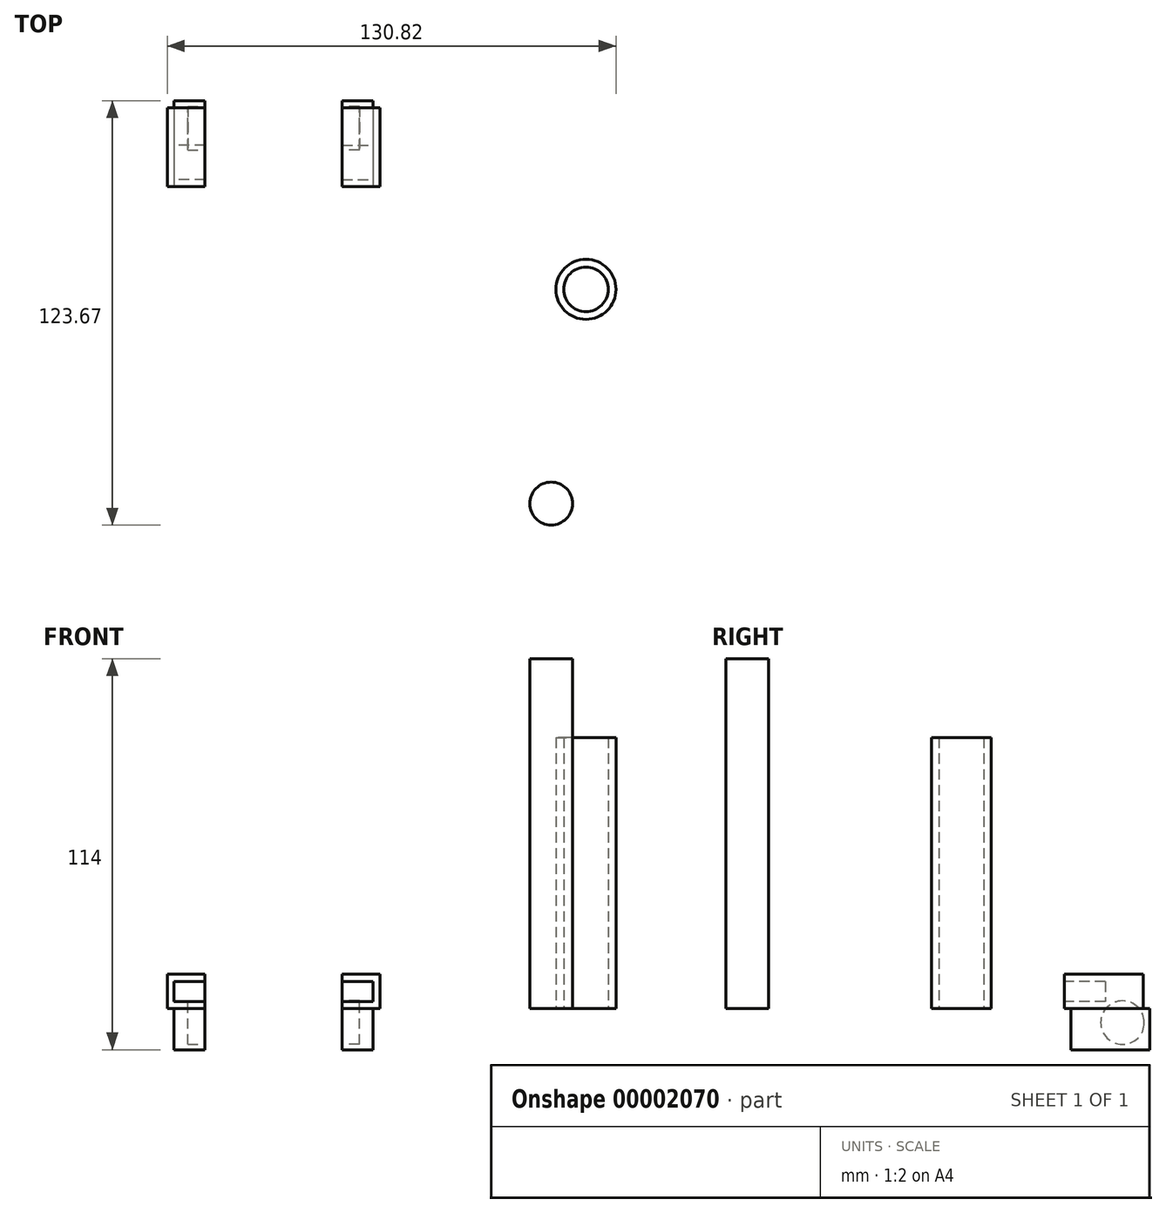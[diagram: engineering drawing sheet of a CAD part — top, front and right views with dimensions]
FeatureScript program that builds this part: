
annotation { "Feature Type Name" : "Feature", "Feature Type Description" : "" }
export const myFeature = defineFeature(function(context is Context, id is Id, definition is map)
    precondition{}
    {
        {
            var Q0;
            Q0=qCreatedBy(makeId("Top.planeOp"),FACE);
            var sketch = newSketch(context, id + "F0", { "sketchPlane" : qUnion([Q0])});
            skLineSegment(sketch, "E0.bottom", {"start": v(-59.77, 61) * mm, "end": v(-48.77, 61) * mm});
            skLineSegment(sketch, "E0.top", {"start": v(-59.77, 46) * mm, "end": v(-48.77, 46) * mm});
            skLineSegment(sketch, "E0.left", {"start": v(-59.77, 61) * mm, "end": v(-59.77, 46) * mm});
            skLineSegment(sketch, "E0.right", {"start": v(-48.77, 61) * mm, "end": v(-48.77, 46) * mm});
            skSolve(sketch);
        }
        {
            var Q0;
            Q0=makeQuery(id+"F0.imprint","IMPRINT",FACE,{"disambiguationData":[TD([[makeQuery(id+"F0.imprint","IMPRINT",EDGE,{"derivedFrom":sQuery(id+"F0.wireOp",EDGE,"E0.bottom")}),-1.0]])]});
            extrude(context, id + "F1", {"entities" : qUnion([Q0]), "depth" : 10 * mm});
        }
        {
            var Q0;
            Q0=makeQuery(id+"F1.opExtrude","SWEPT_FACE",FACE,{"disambiguationData":[OSD([sQuery(id+"F0.wireOp",EDGE,"E0.top")])]});
            var sketch = newSketch(context, id + "F2", { "sketchPlane" : qUnion([Q0])});
            skPoint(sketch, "E1", {"position": v(-48.77, 5) * mm});
            skLineSegment(sketch, "E2", {"start": v(-48.77, 5) * mm, "end": v(-48.77, 7.9) * mm});
            skLineSegment(sketch, "E3", {"start": v(-48.77, 5) * mm, "end": v(-48.77, 2.1) * mm});
            skLineSegment(sketch, "E4", {"start": v(-48.77, 7.9) * mm, "end": v(-57.77, 7.9) * mm});
            skLineSegment(sketch, "E5", {"start": v(-57.77, 7.9) * mm, "end": v(-57.77, 2.1) * mm});
            skLineSegment(sketch, "E6", {"start": v(-57.77, 2.1) * mm, "end": v(-48.77, 2.1) * mm});
            skSolve(sketch);
        }
        {
            var Q0;
            Q0=makeQuery(id+"F2.imprint","IMPRINT",FACE,{"disambiguationData":[TD([[makeQuery(id+"F2.imprint","IMPRINT",EDGE,{"derivedFrom":sQuery(id+"F2.wireOp",EDGE,"E2")}),-1.0]])]});
            extrude(context, id + "F3", {"entities" : qUnion([Q0]), "operationType" : NewBodyOperationType.REMOVE, "oppositeDirection" : true, "depth" : 12 * mm});
        }
        {
            var Q0;
            Q0=makeQuery(id+"F1.opExtrude","CAP_FACE",FACE,{"disambiguationData":[OSD([sQuery(id+"F0.wireOp",EDGE,"E0.bottom"),sQuery(id+"F0.wireOp",EDGE,"E0.top"),sQuery(id+"F0.wireOp",EDGE,"E0.left"),sQuery(id+"F0.wireOp",EDGE,"E0.right")])],"isStart":true});
            var sketch = newSketch(context, id + "F4", { "sketchPlane" : qUnion([Q0])});
            skPoint(sketch, "E7", {"position": v(-48.77, -58) * mm});
            skPoint(sketch, "E8", {"position": v(-57.77, -58) * mm});
            skLineSegment(sketch, "E9.top", {"start": v(-48.77, -48) * mm, "end": v(-57.77, -48) * mm});
            skLineSegment(sketch, "E9.left", {"start": v(-48.77, -58) * mm, "end": v(-48.77, -48) * mm});
            skLineSegment(sketch, "E9.right", {"start": v(-57.77, -58) * mm, "end": v(-57.77, -48) * mm});
            skLineSegment(sketch, "E10", {"start": v(-48.77, -58) * mm, "end": v(-48.77, -63) * mm});
            skLineSegment(sketch, "E11", {"start": v(-48.77, -63) * mm, "end": v(-48.77, -71) * mm});
            skLineSegment(sketch, "E12", {"start": v(-48.77, -71) * mm, "end": v(-57.77, -71) * mm});
            skLineSegment(sketch, "E13", {"start": v(-57.77, -71) * mm, "end": v(-57.77, -57.53) * mm});
            skSolve(sketch);
        }
        {
            var Q0;
            {var subQ5=sQuery(id+"F4.wireOp",EDGE,"E12");Q0=makeQuery(id+"F4.imprint","IMPRINT",FACE,{"disambiguationData":[TD([[makeQuery(id+"F4.imprint","IMPRINT",EDGE,{"derivedFrom":subQ5}),-1.0]])]});}
            var Q1;
            Q1=makeQuery(id+"F4.imprint","IMPRINT",FACE,{"disambiguationData":[TD([[makeQuery(id+"F4.imprint","IMPRINT",EDGE,{"derivedFrom":sQuery(id+"F4.wireOp",EDGE,"E9.top")}),1.0]])]});
            extrude(context, id + "F5", {"entities" : qUnion([Q0, Q1]), "operationType" : NewBodyOperationType.ADD, "depth" : 12 * mm});
        }
        {
            var Q0;
            Q0=makeQuery(id+"F5.boolean.opBoolean","MERGE",FACE,{"derivedFrom":[makeQuery(id+"F1.opExtrude","SWEPT_FACE",FACE,{"disambiguationData":[OSD([sQuery(id+"F0.wireOp",EDGE,"E0.right")])]}),makeQuery(id+"F5.opExtrude","SWEPT_FACE",FACE,{"disambiguationData":[OSD([sQuery(id+"F4.wireOp",EDGE,"E9.left"),sQuery(id+"F4.wireOp",EDGE,"E10")])]})]});
            var sketch = newSketch(context, id + "F6", { "sketchPlane" : qUnion([Q0])});
            skPoint(sketch, "E14", {"position": v(58, -4.1) * mm});
            skPoint(sketch, "E15", {"position": v(58, 7.9) * mm});
            skPoint(sketch, "E16", {"position": v(48, 7.9) * mm});
            skPoint(sketch, "E17", {"position": v(63, 7.9) * mm});
            skPoint(sketch, "E18", {"position": v(63, -4.1) * mm});
            skPoint(sketch, "E19", {"position": v(48, -4.1) * mm});
            skCircle(sketch, "E20", {"center": v(63, -4.1) * mm, "radius": 6.35 * mm});
            skCircle(sketch, "E21", {"center": v(63, -4.1) * mm, "radius": 8.75 * mm, "construction": true});
            skSolve(sketch);
        }
        {
            var Q0;
            Q0=makeQuery(id+"F1.opExtrude","SWEPT_FACE",FACE,{"disambiguationData":[OSD([sQuery(id+"F0.wireOp",EDGE,"E0.bottom")])]});
            extrude(context, id + "F7", {"entities" : qUnion([Q0]), "operationType" : NewBodyOperationType.ADD, "depth" : 8 * mm});
        }
        {
            var Q0;
            {var subQ1=sQuery(id+"F6.wireOp",EDGE,"E20");var subQ3=makeQuery(id+"F1.opExtrude","SWEPT_EDGE",EDGE,{"disambiguationData":[OSD([sQuery(id+"F0.wireOp",EDGE,"E0.bottom"),sQuery(id+"F0.wireOp",EDGE,"E0.right")])]});var subQ5=makeQuery(id+"F6.imprint","INTERSECT",VERTEX,{"derivedFrom":[subQ3,subQ1]});Q0=makeQuery(id+"F6.imprint","IMPRINT",FACE,{"disambiguationData":[TD([[makeQuery(id+"F6.imprint","IMPRINT",EDGE,{"disambiguationData":[TD([[subQ5,-1.0]])],"derivedFrom":subQ1}),1.0]])]});}
            var Q1;
            {var subQ1=sQuery(id+"F6.wireOp",EDGE,"E20");var subQ3=makeQuery(id+"F1.opExtrude","SWEPT_EDGE",EDGE,{"disambiguationData":[OSD([sQuery(id+"F0.wireOp",EDGE,"E0.bottom"),sQuery(id+"F0.wireOp",EDGE,"E0.right")])]});var subQ5=makeQuery(id+"F6.imprint","INTERSECT",VERTEX,{"derivedFrom":[subQ3,subQ1]});Q1=makeQuery(id+"F6.imprint","IMPRINT",FACE,{"disambiguationData":[TD([[makeQuery(id+"F6.imprint","IMPRINT",EDGE,{"disambiguationData":[TD([[subQ5,1.0]])],"derivedFrom":subQ1}),1.0]])]});}
            extrude(context, id + "F8", {"entities" : qUnion([Q0, Q1]), "operationType" : NewBodyOperationType.REMOVE, "oppositeDirection" : true, "depth" : 5 * mm});
        }
        {
            var Q0;
            {var subQ0=sQuery(id+"F0.wireOp",EDGE,"E0.right");Q0=makeQuery(id+"F7.boolean.opBoolean","MERGE",FACE,{"derivedFrom":[makeQuery(id+"F5.boolean.opBoolean","MERGE",FACE,{"derivedFrom":[makeQuery(id+"F1.opExtrude","SWEPT_FACE",FACE,{"disambiguationData":[OSD([subQ0])]}),makeQuery(id+"F5.opExtrude","SWEPT_FACE",FACE,{"disambiguationData":[OSD([sQuery(id+"F4.wireOp",EDGE,"E9.left"),sQuery(id+"F4.wireOp",EDGE,"E10")])]})]}),makeQuery(id+"F7.opExtrude","SWEPT_FACE",FACE,{"disambiguationData":[OSD([sQuery(id+"F0.wireOp",EDGE,"E0.bottom"),subQ0])]})]});}
            cPlane(context, id + "F9", {"entities" : qUnion([Q0]), "cplaneType" : CPlaneType.OFFSET, "offset" : 20 * mm, "width" : 150 * mm, "height" : 150 * mm});
        }
        {
            var Q0;
            Q0=makeQuery(id+"F1.opExtrude","SWEPT_BODY",BODY,{"disambiguationData":[OSD([sQuery(id+"F0.wireOp",EDGE,"E0.bottom"),sQuery(id+"F0.wireOp",EDGE,"E0.top"),sQuery(id+"F0.wireOp",EDGE,"E0.left"),sQuery(id+"F0.wireOp",EDGE,"E0.right")])]});
            var Q1;
            Q1=qCreatedBy(id+"F9.planeOp",FACE);
            mirror(context, id + "F10", {"entities" : qUnion([Q0]), "mirrorPlane" : qUnion([Q1])});
        }
        {
            var Q0;
            Q0=qCreatedBy(makeId("Top.planeOp"),FACE);
            var sketch = newSketch(context, id + "F11", { "sketchPlane" : qUnion([Q0])});
            skCircle(sketch, "E22", {"center": v(52.16, -46.42) * mm, "radius": 6.25 * mm});
            skSolve(sketch);
        }
        {
            var Q0;
            Q0=makeQuery(id+"F11.imprint","IMPRINT",FACE,{"disambiguationData":[TD([[makeQuery(id+"F11.imprint","IMPRINT",EDGE,{"derivedFrom":sQuery(id+"F11.wireOp",EDGE,"E22")}),1.0]])]});
            extrude(context, id + "F12", {"entities" : qUnion([Q0]), "depth" : 102 * mm});
        }
        {
            var Q0;
            Q0=qCreatedBy(makeId("Top.planeOp"),FACE);
            var sketch = newSketch(context, id + "F13", { "sketchPlane" : qUnion([Q0])});
            skCircle(sketch, "E23", {"center": v(62.3, 16.04) * mm, "radius": 8.75 * mm});
            skCircle(sketch, "E24", {"center": v(62.3, 16.04) * mm, "radius": 6.5 * mm});
            skSolve(sketch);
        }
        {
            var Q0;
            Q0=makeQuery(id+"F13.imprint","IMPRINT",FACE,{"disambiguationData":[TD([[makeQuery(id+"F13.imprint","IMPRINT",EDGE,{"derivedFrom":sQuery(id+"F13.wireOp",EDGE,"E23")}),1.0]])]});
            extrude(context, id + "F14", {"entities" : qUnion([Q0]), "depth" : 79 * mm});
        }
    });
